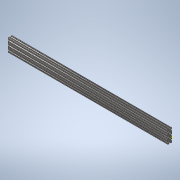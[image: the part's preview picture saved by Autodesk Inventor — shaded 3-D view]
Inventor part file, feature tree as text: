
AUTODESK INVENTOR PART (.ipt)
format: ipt  version: 2020 (Build 240168000, 168)  size: 399,872 bytes
history: native  units: in
note: dims shown in document units (in); Inventor stores cm internally (conversion verified against a paired STEP export)
features: sketch x2, extrude x1
ambient origin geometry x8: Origin, YZ Plane, XZ Plane, XY Plane, X Axis, Y Axis, Z Axis, Center Point
bodies: Solid1 (feature_tree)
feature tree (3):
  extrude  "Extrusion1"  [1 undecoded]
  sketch  "Sketch2"
  sketch  "Sketch1"  dims[d0=37.0in d1=0.0in]
note: 1 required parameter value undecoded (feature->parameter linkage not recoverable at this tier; creation-order binding heuristic only, values carry confidence <= 0.55)
